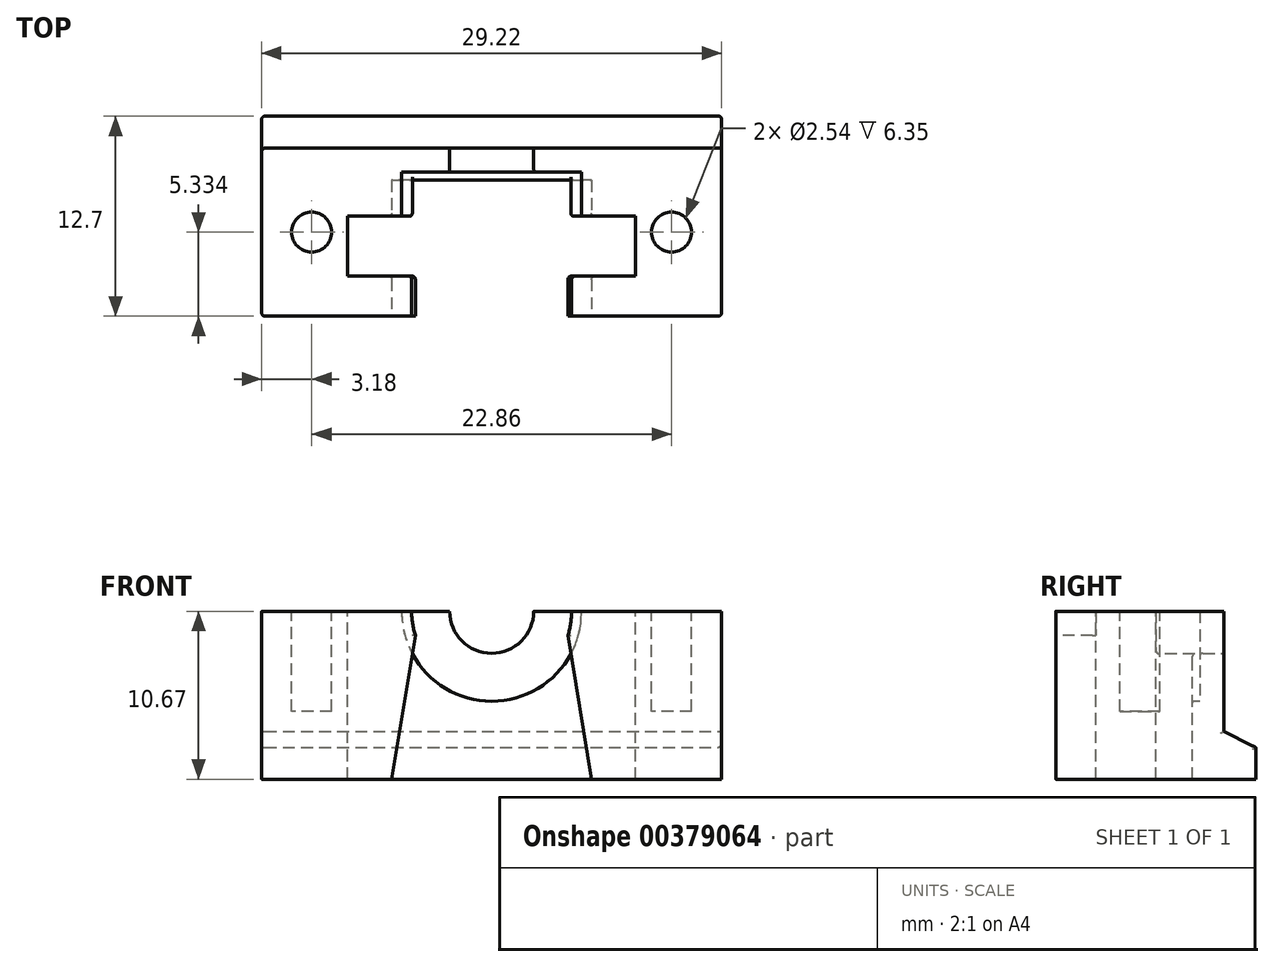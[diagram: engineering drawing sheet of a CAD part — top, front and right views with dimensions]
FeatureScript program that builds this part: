
annotation { "Feature Type Name" : "Feature", "Feature Type Description" : "" }
export const myFeature = defineFeature(function(context is Context, id is Id, definition is map)
    precondition{}
    {
        {
            var Q0;
            Q0=qCreatedBy(makeId("Front.planeOp"),FACE);
            var sketch = newSketch(context, id + "F0", { "sketchPlane" : qUnion([Q0])});
            skLineSegment(sketch, "E0.bottom", {"start": v(14.6, -3.75) * mm, "end": v(-14.6, -3.75) * mm});
            skLineSegment(sketch, "E0.left", {"start": v(14.6, -3.75) * mm, "end": v(14.6, 3.75) * mm});
            skLineSegment(sketch, "E0.right", {"start": v(-14.6, -3.75) * mm, "end": v(-14.6, 3.75) * mm});
            skPoint(sketch, "E0.middle", {"position": v(0, 0) * mm});
            skArc(sketch, "E1", {"start": v(14.6, 3.75) * mm, "mid": v(0, 18.35) * mm, "end": v(-14.6, 3.75) * mm, "construction": true});
            skPoint(sketch, "E2", {"position": v(0, 18.35) * mm});
            skLineSegment(sketch, "E3", {"start": v(-14.6, 3.75) * mm, "end": v(-14.6, 18.35) * mm});
            skLineSegment(sketch, "E4", {"start": v(-14.6, 18.35) * mm, "end": v(14.6, 18.35) * mm});
            skLineSegment(sketch, "E5", {"start": v(14.6, 18.35) * mm, "end": v(14.6, 3.75) * mm});
            skSolve(sketch);
        }
        {
            var Q0;
            Q0=qSketchRegion(id+"F0",true);
            extrude(context, id + "F1", {"entities" : qUnion([Q0]), "depth" : 12.7 * mm});
        }
        {
            var Q0;
            Q0=qCreatedBy(makeId("Front.planeOp"),FACE);
            cPlane(context, id + "F2", {"entities" : qUnion([Q0]), "cplaneType" : CPlaneType.OFFSET, "offset" : 6.35 * mm, "width" : 152.4 * mm, "height" : 152.4 * mm});
        }
        {
            var Q0;
            Q0=qCreatedBy(id+"F2.planeOp",FACE);
            var sketch = newSketch(context, id + "F3", { "sketchPlane" : qUnion([Q0])});
            skLineSegment(sketch, "E6.bottom", {"start": v(9.14, -3.75) * mm, "end": v(-9.14, -3.75) * mm});
            skLineSegment(sketch, "E6.left", {"start": v(9.14, -3.75) * mm, "end": v(9.14, 6.92) * mm});
            skLineSegment(sketch, "E6.right", {"start": v(-9.14, -3.75) * mm, "end": v(-9.14, 6.92) * mm});
            skLineSegment(sketch, "E7", {"start": v(0, -3.75) * mm, "end": v(0, 19.01) * mm, "construction": true});
            skArc(sketch, "E8", {"start": v(9.14, 6.92) * mm, "mid": v(0, 16.07) * mm, "end": v(-9.14, 6.92) * mm});
            skPoint(sketch, "E9", {"position": v(0, 16.07) * mm});
            skSolve(sketch);
        }
        {
            var Q0;
            Q0=qSketchRegion(id+"F3",true);
            extrude(context, id + "F4", {"entities" : qUnion([Q0]), "operationType" : NewBodyOperationType.REMOVE, "depth" : 3.8 * mm});
        }
        {
            var Q0;
            Q0=makeQuery(id+"F1.opExtrude","CAP_FACE",FACE,{"disambiguationData":[OSD([sQuery(id+"F0.wireOp",EDGE,"E0.bottom"),sQuery(id+"F0.wireOp",EDGE,"E0.left"),sQuery(id+"F0.wireOp",EDGE,"E0.right"),sQuery(id+"F0.wireOp",EDGE,"E1")])],"isStart":false});
            var sketch = newSketch(context, id + "F5", { "sketchPlane" : qUnion([Q0])});
            skArc(sketch, "E10", {"start": v(4.85, 5.4) * mm, "mid": v(0, 12) * mm, "end": v(-4.85, 5.4) * mm});
            skLineSegment(sketch, "E11", {"start": v(4.85, 5.4) * mm, "end": v(-4.85, 5.4) * mm, "construction": true});
            skLineSegment(sketch, "E12", {"start": v(4.85, 5.4) * mm, "end": v(6.35, -3.75) * mm});
            skLineSegment(sketch, "E13", {"start": v(6.35, -3.75) * mm, "end": v(-6.35, -3.75) * mm});
            skLineSegment(sketch, "E14", {"start": v(-6.35, -3.75) * mm, "end": v(-4.85, 5.4) * mm});
            skLineSegment(sketch, "E15", {"start": v(0, -3.75) * mm, "end": v(0, 6.92) * mm, "construction": true});
            skSolve(sketch);
        }
        {
            var Q0;
            Q0=qSketchRegion(id+"F5",true);
            extrude(context, id + "F6", {"entities" : qUnion([Q0]), "operationType" : NewBodyOperationType.REMOVE, "oppositeDirection" : true, "depth" : 8.64 * mm});
        }
        {
            var Q0;
            Q0=makeQuery(id+"F1.opExtrude","SWEPT_FACE",FACE,{"disambiguationData":[OSD([sQuery(id+"F0.wireOp",EDGE,"E0.left")])]});
            var sketch = newSketch(context, id + "F7", { "sketchPlane" : qUnion([Q0])});
            skLineSegment(sketch, "E16", {"start": v(0, -1.71) * mm, "end": v(-2.03, -0.7) * mm});
            skLineSegment(sketch, "E17", {"start": v(-2.03, -0.7) * mm, "end": v(-2.03, 15.3) * mm});
            skLineSegment(sketch, "E18", {"start": v(-2.03, 15.3) * mm, "end": v(0, 16.32) * mm});
            skLineSegment(sketch, "E19", {"start": v(0, 16.32) * mm, "end": v(0, -1.71) * mm});
            skLineSegment(sketch, "E20", {"start": v(-2.03, 7.3) * mm, "end": v(0, 7.3) * mm, "construction": true});
            skPoint(sketch, "E20.startSnap0", {"position": v(0, 7.3) * mm});
            skSolve(sketch);
        }
        {
            var Q0;
            Q0=qSketchRegion(id+"F7",true);
            extrude(context, id + "F8", {"entities" : qUnion([Q0]), "operationType" : NewBodyOperationType.REMOVE, "endBound" : BoundingType.THROUGH_ALL, "oppositeDirection" : true, "depth" : 25.4 * mm});
        }
        {
            var Q0;
            Q0=makeQuery(id+"F8.boolean.opBoolean","COPY",FACE,{"derivedFrom":makeQuery(id+"F8.opExtrude","SWEPT_FACE",FACE,{"disambiguationData":[OSD([sQuery(id+"F7.wireOp",EDGE,"E17")])]})});
            var sketch = newSketch(context, id + "F9", { "sketchPlane" : qUnion([Q0])});
            skCircle(sketch, "E21", {"center": v(0, 6.92) * mm, "radius": 2.67 * mm});
            skSolve(sketch);
        }
        {
            var Q0;
            Q0=qSketchRegion(id+"F9",true);
            var Q1;
            Q1=qCreatedBy(id+"F2.planeOp",FACE);
            extrude(context, id + "F10", {"entities" : qUnion([Q0]), "operationType" : NewBodyOperationType.REMOVE, "endBound" : BoundingType.UP_TO_SURFACE, "oppositeDirection" : true, "endBoundEntityFace" : qUnion([Q1]), "depth" : 25.4 * mm});
        }
        {
            var Q0;
            Q0=makeQuery(id+"F1.opExtrude","SWEPT_FACE",FACE,{"disambiguationData":[OSD([sQuery(id+"F0.wireOp",EDGE,"E4")])]});
            var sketch = newSketch(context, id + "F11", { "sketchPlane" : qUnion([Q0])});
            skLineSegment(sketch, "E22", {"start": v(14.6, -7.37) * mm, "end": v(-14.6, -7.37) * mm, "construction": true});
            skArc(sketch, "E23", {"start": v(11.43, -4.2) * mm, "mid": v(8.25, -7.37) * mm, "end": v(11.43, -10.54) * mm});
            skLineSegment(sketch, "E24", {"start": v(0, -12.7) * mm, "end": v(0, 0) * mm, "construction": true});
            skLineSegment(sketch, "E25", {"start": v(11.43, -4.2) * mm, "end": v(14.6, -4.2) * mm});
            skLineSegment(sketch, "E26", {"start": v(14.6, -4.2) * mm, "end": v(14.6, -10.54) * mm});
            skLineSegment(sketch, "E27", {"start": v(14.6, -10.54) * mm, "end": v(11.43, -10.54) * mm});
            skLineSegment(sketch, "E28", {"start": v(11.43, -4.2) * mm, "end": v(11.43, -10.54) * mm, "construction": true});
            skArc(sketch, "E29.MirrorCS", {"start": v(-11.43, -4.2) * mm, "mid": v(-8.26, -7.37) * mm, "end": v(-11.43, -10.54) * mm});
            skLineSegment(sketch, "E30.MirrorCS", {"start": v(-11.43, -4.2) * mm, "end": v(-14.6, -4.2) * mm});
            skLineSegment(sketch, "E31.MirrorCS", {"start": v(-14.6, -10.54) * mm, "end": v(-11.43, -10.54) * mm});
            skLineSegment(sketch, "E32.MirrorCS", {"start": v(-14.6, -4.2) * mm, "end": v(-14.6, -10.54) * mm});
            skSolve(sketch);
        }
        {
            var Q0;
            Q0=qSketchRegion(id+"F11",true);
            extrude(context, id + "F12", {"entities" : qUnion([Q0]), "operationType" : NewBodyOperationType.REMOVE, "oppositeDirection" : true, "depth" : 5.08 * mm});
        }
        {
            var Q0;
            Q0=makeQuery(id+"F12.boolean.opBoolean","COPY",FACE,{"derivedFrom":makeQuery(id+"F12.opExtrude","CAP_FACE",FACE,{"disambiguationData":[OSD([sQuery(id+"F11.wireOp",EDGE,"E23")])],"isStart":false})});
            var sketch = newSketch(context, id + "F13", { "sketchPlane" : qUnion([Q0])});
            skCircle(sketch, "E33", {"center": v(11.43, -7.37) * mm, "radius": 1.27 * mm});
            skCircle(sketch, "E34", {"center": v(-11.43, -7.37) * mm, "radius": 1.27 * mm});
            skSolve(sketch);
        }
        {
            var Q0;
            Q0=qSketchRegion(id+"F13",true);
            extrude(context, id + "F14", {"entities" : qUnion([Q0]), "operationType" : NewBodyOperationType.REMOVE, "oppositeDirection" : true, "depth" : 12.7 * mm});
        }
        {
            var Q0;
            Q0=makeQuery(id+"F4.boolean.opBoolean","COPY",FACE,{"derivedFrom":makeQuery(id+"F4.opExtrude","CAP_FACE",FACE,{"disambiguationData":[OSD([sQuery(id+"F3.wireOp",EDGE,"E6.bottom"),sQuery(id+"F3.wireOp",EDGE,"E6.left"),sQuery(id+"F3.wireOp",EDGE,"E6.right"),sQuery(id+"F3.wireOp",EDGE,"E8")])],"isStart":true})});
            var sketch = newSketch(context, id + "F15", { "sketchPlane" : qUnion([Q0])});
            skCircle(sketch, "E35", {"center": v(0, 6.92) * mm, "radius": 5.72 * mm});
            skSolve(sketch);
        }
        {
            var Q0;
            Q0=qSketchRegion(id+"F15",true);
            extrude(context, id + "F16", {"entities" : qUnion([Q0]), "operationType" : NewBodyOperationType.REMOVE, "oppositeDirection" : true, "depth" : 2.8 * mm});
        }
        {
            var Q0;
            Q0=makeQuery(id+"F1.opExtrude","SWEPT_FACE",FACE,{"disambiguationData":[OSD([sQuery(id+"F0.wireOp",EDGE,"E4")])]});
            var sketch = newSketch(context, id + "F17", { "sketchPlane" : qUnion([Q0])});
            skLineSegment(sketch, "E36.bottom", {"start": v(-14.6, 0) * mm, "end": v(14.6, 0) * mm});
            skLineSegment(sketch, "E36.top", {"start": v(-14.6, -12.7) * mm, "end": v(14.6, -12.7) * mm});
            skLineSegment(sketch, "E36.left", {"start": v(-14.6, 0) * mm, "end": v(-14.6, -12.7) * mm});
            skLineSegment(sketch, "E36.right", {"start": v(14.6, 0) * mm, "end": v(14.6, -12.7) * mm});
            skSolve(sketch);
        }
        {
            var Q0;
            Q0 = qSketchRegion(id + "F17", true);
            extrude(context, id + "F18", {"entities" : qUnion([Q0]), "operationType" : NewBodyOperationType.REMOVE, "oppositeDirection" : true, "depth" : 11.43 * mm});
        }
        {
            var Q0;
            Q0=makeQuery(id+"F1.opExtrude","CAP_EDGE",EDGE,{"disambiguationData":[OSD([sQuery(id+"F0.wireOp",EDGE,"E0.left"),sQuery(id+"F0.wireOp",EDGE,"E5")])],"isStart":false});
            var Q1;
            {var subQ2=makeQuery(id+"F4.boolean.opBoolean","COPY",FACE,{"derivedFrom":makeQuery(id+"F4.opExtrude","CAP_FACE",FACE,{"disambiguationData":[OSD([sQuery(id+"F3.wireOp",EDGE,"E6.bottom"),sQuery(id+"F3.wireOp",EDGE,"E6.left"),sQuery(id+"F3.wireOp",EDGE,"E6.right"),sQuery(id+"F3.wireOp",EDGE,"E8")])],"isStart":false})});var subQ3=makeQuery(id+"F6.opExtrude","SWEPT_FACE",FACE,{"disambiguationData":[OSD([sQuery(id+"F5.wireOp",EDGE,"E12")])]});var subQ4=sQuery(id+"F5.wireOp",EDGE,"E10");Q1=makeQuery(id+"F18.boolean.opBoolean","SPLIT",EDGE,{"disambiguationData":[TD([makeQuery(id+"F6.boolean.opBoolean","COPY",FACE,{"disambiguationData":[TD([subQ2])],"derivedFrom":subQ3})])],"derivedFrom":makeQuery(id+"F6.boolean.opBoolean","COPY",EDGE,{"derivedFrom":makeQuery(id+"F6.opExtrude","CAP_EDGE",EDGE,{"disambiguationData":[OSD([subQ4])],"isStart":true})})});}
            var Q2;
            Q2=makeQuery(id+"F6.boolean.opBoolean","COPY",EDGE,{"derivedFrom":makeQuery(id+"F6.opExtrude","CAP_EDGE",EDGE,{"disambiguationData":[OSD([sQuery(id+"F5.wireOp",EDGE,"E12")])],"isStart":true})});
            var Q3;
            {var subQ0=makeQuery(id+"F4.boolean.opBoolean","COPY",FACE,{"derivedFrom":makeQuery(id+"F4.opExtrude","CAP_FACE",FACE,{"disambiguationData":[OSD([sQuery(id+"F3.wireOp",EDGE,"E6.bottom"),sQuery(id+"F3.wireOp",EDGE,"E6.left"),sQuery(id+"F3.wireOp",EDGE,"E6.right"),sQuery(id+"F3.wireOp",EDGE,"E8")])],"isStart":false})});var subQ3=makeQuery(id+"F6.opExtrude","SWEPT_FACE",FACE,{"disambiguationData":[OSD([sQuery(id+"F5.wireOp",EDGE,"E10")])]});var subQ4=makeQuery(id+"F6.opExtrude","SWEPT_FACE",FACE,{"disambiguationData":[OSD([sQuery(id+"F5.wireOp",EDGE,"E12")])]});Q3=makeQuery(id+"F18.boolean.opBoolean","SPLIT",EDGE,{"disambiguationData":[TD([makeQuery(id+"F6.boolean.opBoolean","COPY",FACE,{"disambiguationData":[TD([subQ0])],"derivedFrom":subQ4})])],"derivedFrom":makeQuery(id+"F6.boolean.opBoolean","INTERSECT",EDGE,{"derivedFrom":[subQ0,subQ3]})});}
            var Q4;
            Q4=makeQuery(id+"F6.boolean.opBoolean","INTERSECT",EDGE,{"derivedFrom":[makeQuery(id+"F4.boolean.opBoolean","COPY",FACE,{"derivedFrom":makeQuery(id+"F4.opExtrude","CAP_FACE",FACE,{"disambiguationData":[OSD([sQuery(id+"F3.wireOp",EDGE,"E6.bottom"),sQuery(id+"F3.wireOp",EDGE,"E6.left"),sQuery(id+"F3.wireOp",EDGE,"E6.right"),sQuery(id+"F3.wireOp",EDGE,"E8")])],"isStart":false})}),makeQuery(id+"F6.opExtrude","SWEPT_FACE",FACE,{"disambiguationData":[OSD([sQuery(id+"F5.wireOp",EDGE,"E12")])]})]});
            var Q5;
            {var subQ0=makeQuery(id+"F4.boolean.opBoolean","COPY",FACE,{"derivedFrom":makeQuery(id+"F4.opExtrude","CAP_FACE",FACE,{"disambiguationData":[OSD([sQuery(id+"F3.wireOp",EDGE,"E6.bottom"),sQuery(id+"F3.wireOp",EDGE,"E6.left"),sQuery(id+"F3.wireOp",EDGE,"E6.right"),sQuery(id+"F3.wireOp",EDGE,"E8")])],"isStart":true})});var subQ1=sQuery(id+"F5.wireOp",EDGE,"E12");var subQ3=sQuery(id+"F15.wireOp",EDGE,"E35");Q5=makeQuery(id+"F18.boolean.opBoolean","SPLIT",EDGE,{"disambiguationData":[TD([makeQuery(id+"F6.boolean.opBoolean","COPY",FACE,{"disambiguationData":[TD([subQ0])],"derivedFrom":makeQuery(id+"F6.opExtrude","SWEPT_FACE",FACE,{"disambiguationData":[OSD([subQ1])]})})])],"derivedFrom":makeQuery(id+"F16.boolean.opBoolean","COPY",EDGE,{"derivedFrom":makeQuery(id+"F16.opExtrude","CAP_EDGE",EDGE,{"disambiguationData":[OSD([subQ3])],"isStart":true})})});}
            var Q6;
            Q6=makeQuery(id+"F6.boolean.opBoolean","INTERSECT",EDGE,{"derivedFrom":[makeQuery(id+"F4.boolean.opBoolean","COPY",FACE,{"derivedFrom":makeQuery(id+"F4.opExtrude","CAP_FACE",FACE,{"disambiguationData":[OSD([sQuery(id+"F3.wireOp",EDGE,"E6.bottom"),sQuery(id+"F3.wireOp",EDGE,"E6.left"),sQuery(id+"F3.wireOp",EDGE,"E6.right"),sQuery(id+"F3.wireOp",EDGE,"E8")])],"isStart":true})}),makeQuery(id+"F6.opExtrude","SWEPT_FACE",FACE,{"disambiguationData":[OSD([sQuery(id+"F5.wireOp",EDGE,"E12")])]})]});
            var Q7;
            {var subQ2=makeQuery(id+"F4.boolean.opBoolean","COPY",FACE,{"derivedFrom":makeQuery(id+"F4.opExtrude","CAP_FACE",FACE,{"disambiguationData":[OSD([sQuery(id+"F3.wireOp",EDGE,"E6.bottom"),sQuery(id+"F3.wireOp",EDGE,"E6.left"),sQuery(id+"F3.wireOp",EDGE,"E6.right"),sQuery(id+"F3.wireOp",EDGE,"E8")])],"isStart":false})});var subQ3=makeQuery(id+"F6.opExtrude","SWEPT_FACE",FACE,{"disambiguationData":[OSD([sQuery(id+"F5.wireOp",EDGE,"E14")])]});var subQ4=sQuery(id+"F5.wireOp",EDGE,"E10");Q7=makeQuery(id+"F18.boolean.opBoolean","SPLIT",EDGE,{"disambiguationData":[TD([makeQuery(id+"F6.boolean.opBoolean","COPY",FACE,{"disambiguationData":[TD([subQ2])],"derivedFrom":subQ3})])],"derivedFrom":makeQuery(id+"F6.boolean.opBoolean","COPY",EDGE,{"derivedFrom":makeQuery(id+"F6.opExtrude","CAP_EDGE",EDGE,{"disambiguationData":[OSD([subQ4])],"isStart":true})})});}
            var Q8;
            {var subQ0=makeQuery(id+"F4.boolean.opBoolean","COPY",FACE,{"derivedFrom":makeQuery(id+"F4.opExtrude","CAP_FACE",FACE,{"disambiguationData":[OSD([sQuery(id+"F3.wireOp",EDGE,"E6.bottom"),sQuery(id+"F3.wireOp",EDGE,"E6.left"),sQuery(id+"F3.wireOp",EDGE,"E6.right"),sQuery(id+"F3.wireOp",EDGE,"E8")])],"isStart":false})});var subQ3=makeQuery(id+"F6.opExtrude","SWEPT_FACE",FACE,{"disambiguationData":[OSD([sQuery(id+"F5.wireOp",EDGE,"E14")])]});var subQ4=makeQuery(id+"F6.opExtrude","SWEPT_FACE",FACE,{"disambiguationData":[OSD([sQuery(id+"F5.wireOp",EDGE,"E10")])]});Q8=makeQuery(id+"F18.boolean.opBoolean","SPLIT",EDGE,{"disambiguationData":[TD([makeQuery(id+"F6.boolean.opBoolean","COPY",FACE,{"disambiguationData":[TD([subQ0])],"derivedFrom":subQ3})])],"derivedFrom":makeQuery(id+"F6.boolean.opBoolean","INTERSECT",EDGE,{"derivedFrom":[subQ0,subQ4]})});}
            var Q9;
            Q9=makeQuery(id+"F6.boolean.opBoolean","INTERSECT",EDGE,{"derivedFrom":[makeQuery(id+"F4.boolean.opBoolean","COPY",FACE,{"derivedFrom":makeQuery(id+"F4.opExtrude","CAP_FACE",FACE,{"disambiguationData":[OSD([sQuery(id+"F3.wireOp",EDGE,"E6.bottom"),sQuery(id+"F3.wireOp",EDGE,"E6.left"),sQuery(id+"F3.wireOp",EDGE,"E6.right"),sQuery(id+"F3.wireOp",EDGE,"E8")])],"isStart":false})}),makeQuery(id+"F6.opExtrude","SWEPT_FACE",FACE,{"disambiguationData":[OSD([sQuery(id+"F5.wireOp",EDGE,"E14")])]})]});
            var Q10;
            Q10=makeQuery(id+"F6.boolean.opBoolean","COPY",EDGE,{"derivedFrom":makeQuery(id+"F6.opExtrude","CAP_EDGE",EDGE,{"disambiguationData":[OSD([sQuery(id+"F5.wireOp",EDGE,"E14")])],"isStart":true})});
            var Q11;
            {var subQ0=makeQuery(id+"F4.boolean.opBoolean","COPY",FACE,{"derivedFrom":makeQuery(id+"F4.opExtrude","CAP_FACE",FACE,{"disambiguationData":[OSD([sQuery(id+"F3.wireOp",EDGE,"E6.bottom"),sQuery(id+"F3.wireOp",EDGE,"E6.left"),sQuery(id+"F3.wireOp",EDGE,"E6.right"),sQuery(id+"F3.wireOp",EDGE,"E8")])],"isStart":true})});var subQ1=sQuery(id+"F5.wireOp",EDGE,"E14");var subQ3=sQuery(id+"F15.wireOp",EDGE,"E35");Q11=makeQuery(id+"F18.boolean.opBoolean","SPLIT",EDGE,{"disambiguationData":[TD([makeQuery(id+"F6.boolean.opBoolean","COPY",FACE,{"disambiguationData":[TD([subQ0])],"derivedFrom":makeQuery(id+"F6.opExtrude","SWEPT_FACE",FACE,{"disambiguationData":[OSD([subQ1])]})})])],"derivedFrom":makeQuery(id+"F16.boolean.opBoolean","COPY",EDGE,{"derivedFrom":makeQuery(id+"F16.opExtrude","CAP_EDGE",EDGE,{"disambiguationData":[OSD([subQ3])],"isStart":true})})});}
            var Q12;
            Q12=makeQuery(id+"F6.boolean.opBoolean","INTERSECT",EDGE,{"derivedFrom":[makeQuery(id+"F4.boolean.opBoolean","COPY",FACE,{"derivedFrom":makeQuery(id+"F4.opExtrude","CAP_FACE",FACE,{"disambiguationData":[OSD([sQuery(id+"F3.wireOp",EDGE,"E6.bottom"),sQuery(id+"F3.wireOp",EDGE,"E6.left"),sQuery(id+"F3.wireOp",EDGE,"E6.right"),sQuery(id+"F3.wireOp",EDGE,"E8")])],"isStart":true})}),makeQuery(id+"F6.opExtrude","SWEPT_FACE",FACE,{"disambiguationData":[OSD([sQuery(id+"F5.wireOp",EDGE,"E14")])]})]});
            var Q13;
            Q13=makeQuery(id+"F16.boolean.opBoolean","INTERSECT",EDGE,{"derivedFrom":[makeQuery(id+"F6.boolean.opBoolean","COPY",FACE,{"derivedFrom":makeQuery(id+"F6.opExtrude","CAP_FACE",FACE,{"disambiguationData":[OSD([sQuery(id+"F5.wireOp",EDGE,"E10"),sQuery(id+"F5.wireOp",EDGE,"E12"),sQuery(id+"F5.wireOp",EDGE,"E13"),sQuery(id+"F5.wireOp",EDGE,"E14")])],"isStart":false})}),makeQuery(id+"F16.opExtrude","SWEPT_FACE",FACE,{"disambiguationData":[OSD([sQuery(id+"F15.wireOp",EDGE,"E35")])]})]});
            var Q14;
            Q14=makeQuery(id+"F16.boolean.opBoolean","INTERSECT",EDGE,{"derivedFrom":[makeQuery(id+"F10.boolean.opBoolean","COPY",FACE,{"derivedFrom":makeQuery(id+"F10.opExtrude","SWEPT_FACE",FACE,{"disambiguationData":[OSD([sQuery(id+"F9.wireOp",EDGE,"E21")])]})}),makeQuery(id+"F16.opExtrude","CAP_FACE",FACE,{"disambiguationData":[OSD([sQuery(id+"F15.wireOp",EDGE,"E35")])],"isStart":false})]});
            var Q15;
            Q15=makeQuery(id+"F10.boolean.opBoolean","COPY",EDGE,{"derivedFrom":makeQuery(id+"F10.opExtrude","CAP_EDGE",EDGE,{"disambiguationData":[OSD([sQuery(id+"F9.wireOp",EDGE,"E21")])],"isStart":true})});
            var Q16;
            Q16=makeQuery(id+"F8.boolean.opBoolean","COPY",EDGE,{"derivedFrom":makeQuery(id+"F8.opExtrude","CAP_EDGE",EDGE,{"disambiguationData":[OSD([sQuery(id+"F7.wireOp",EDGE,"E17")])],"isStart":true})});
            var Q17;
            Q17=makeQuery(id+"F8.boolean.opBoolean","INTERSECT",EDGE,{"derivedFrom":[makeQuery(id+"F1.opExtrude","SWEPT_FACE",FACE,{"disambiguationData":[OSD([sQuery(id+"F0.wireOp",EDGE,"E0.right"),sQuery(id+"F0.wireOp",EDGE,"E3")])]}),makeQuery(id+"F8.opExtrude","SWEPT_FACE",FACE,{"disambiguationData":[OSD([sQuery(id+"F7.wireOp",EDGE,"E17")])]})]});
            var Q18;
            Q18=makeQuery(id+"F8.boolean.opBoolean","INTERSECT",EDGE,{"derivedFrom":[makeQuery(id+"F1.opExtrude","SWEPT_FACE",FACE,{"disambiguationData":[OSD([sQuery(id+"F0.wireOp",EDGE,"E0.right"),sQuery(id+"F0.wireOp",EDGE,"E3")])]}),makeQuery(id+"F8.opExtrude","SWEPT_FACE",FACE,{"disambiguationData":[OSD([sQuery(id+"F7.wireOp",EDGE,"E16")])]})]});
            var Q19;
            {var subQ0=sQuery(id+"F0.wireOp",EDGE,"E0.bottom");var subQ1=sQuery(id+"F0.wireOp",EDGE,"E3");var subQ2=sQuery(id+"F0.wireOp",EDGE,"E0.right");Q19=makeQuery(id+"F8.boolean.opBoolean","SPLIT",EDGE,{"disambiguationData":[TD([makeQuery(id+"F1.opExtrude","SWEPT_FACE",FACE,{"disambiguationData":[OSD([subQ0])]})])],"derivedFrom":makeQuery(id+"F1.opExtrude","CAP_EDGE",EDGE,{"disambiguationData":[OSD([subQ2,subQ1])],"isStart":true})});}
            var Q20;
            Q20=makeQuery(id+"F8.boolean.opBoolean","COPY",EDGE,{"derivedFrom":makeQuery(id+"F8.opExtrude","CAP_EDGE",EDGE,{"disambiguationData":[OSD([sQuery(id+"F7.wireOp",EDGE,"E16")])],"isStart":true})});
            var Q21;
            {var subQ0=sQuery(id+"F0.wireOp",EDGE,"E0.bottom");var subQ1=sQuery(id+"F0.wireOp",EDGE,"E5");var subQ2=sQuery(id+"F0.wireOp",EDGE,"E0.left");Q21=makeQuery(id+"F8.boolean.opBoolean","SPLIT",EDGE,{"disambiguationData":[TD([makeQuery(id+"F1.opExtrude","SWEPT_FACE",FACE,{"disambiguationData":[OSD([subQ0])]})])],"derivedFrom":makeQuery(id+"F1.opExtrude","CAP_EDGE",EDGE,{"disambiguationData":[OSD([subQ2,subQ1])],"isStart":true})});}
            var Q22;
            Q22=makeQuery(id+"F1.opExtrude","CAP_EDGE",EDGE,{"disambiguationData":[OSD([sQuery(id+"F0.wireOp",EDGE,"E0.right"),sQuery(id+"F0.wireOp",EDGE,"E3")])],"isStart":false});
            fillet(context, id + "F19", {"entities" : qUnion([Q0, Q1, Q2, Q3, Q4, Q5, Q6, Q7, Q8, Q9, Q10, Q11, Q12, Q13, Q14, Q15, Q16, Q17, Q18, Q19, Q20, Q21, Q22]), "radius" : .2 * mm, "tangentPropagation" : true, "allowEdgeOverflow" : false});
        }
    });
